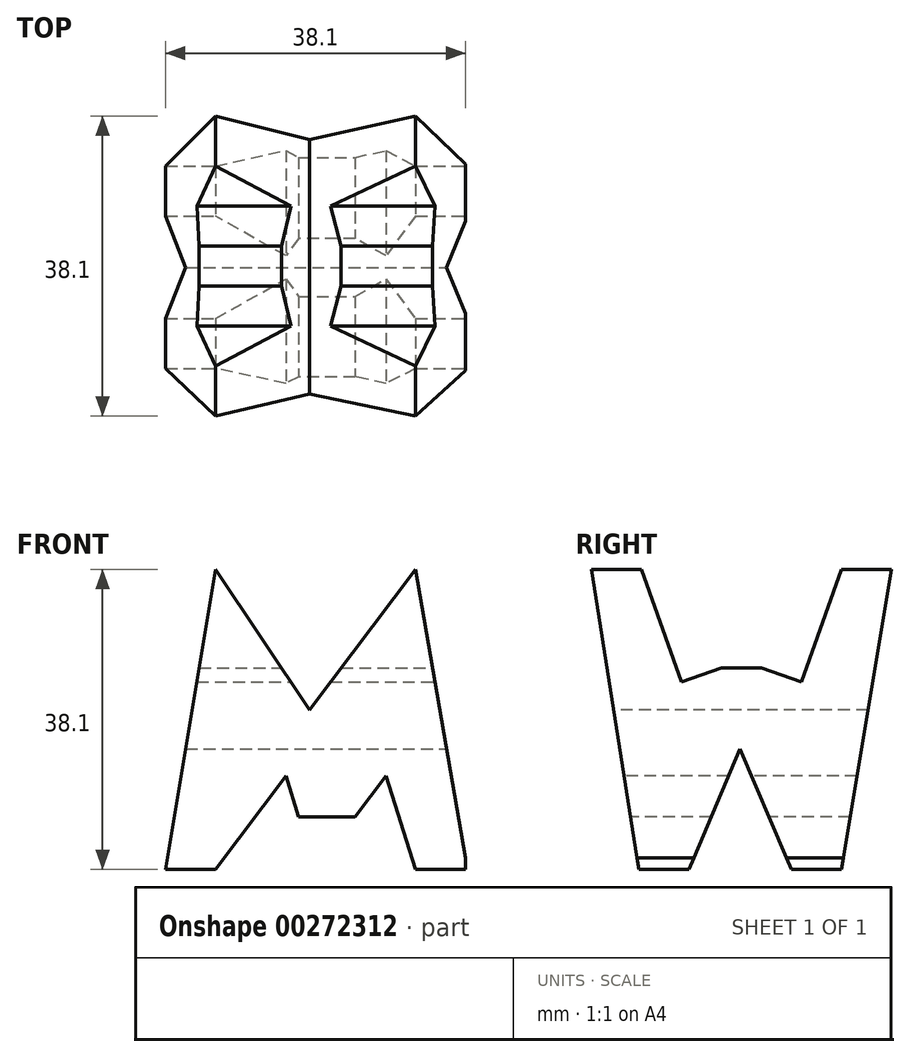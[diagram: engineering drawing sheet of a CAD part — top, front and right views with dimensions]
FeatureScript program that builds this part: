
annotation { "Feature Type Name" : "Feature", "Feature Type Description" : "" }
export const myFeature = defineFeature(function(context is Context, id is Id, definition is map)
    precondition{}
    {
        {
            var Q0;
            Q0=qCreatedBy(makeId("Front.planeOp"),FACE);
            var sketch = newSketch(context, id + "F0", { "sketchPlane" : qUnion([Q0])});
            skLineSegment(sketch, "E0.bottom", {"start": v(0, 0) * mm, "end": v(38.1, 0) * mm});
            skLineSegment(sketch, "E0.top", {"start": v(0, 38.1) * mm, "end": v(38.1, 38.1) * mm});
            skLineSegment(sketch, "E0.left", {"start": v(0, 0) * mm, "end": v(0, 38.1) * mm});
            skLineSegment(sketch, "E0.right", {"start": v(38.1, 0) * mm, "end": v(38.1, 38.1) * mm});
            skSolve(sketch);
        }
        {
            var Q0;
            Q0 = qSketchRegion(id + "F0", true);
            extrude(context, id + "F1", {"entities" : qUnion([Q0]), "depth" : 38.1 * mm});
        }
        {
            var Q0;
            Q0=qCreatedBy(makeId("Front.planeOp"),FACE);
            cPlane(context, id + "F2", {"entities" : qUnion([Q0]), "cplaneType" : CPlaneType.OFFSET, "offset" : 38.1 * mm, "width" : 152.4 * mm, "height" : 152.4 * mm});
        }
        {
            var Q0;
            Q0=qCreatedBy(makeId("Right.planeOp"),FACE);
            cPlane(context, id + "F3", {"entities" : qUnion([Q0]), "cplaneType" : CPlaneType.OFFSET, "offset" : 38.1 * mm, "width" : 152.4 * mm, "height" : 152.4 * mm});
        }
        {
            var Q0;
            Q0=qCreatedBy(id+"F3.planeOp",FACE);
            var sketch = newSketch(context, id + "F4", { "sketchPlane" : qUnion([Q0])});
            skLineSegment(sketch, "E1.bottom", {"start": v(-38.43, 0) * mm, "end": v(0, 0) * mm});
            skLineSegment(sketch, "E1.top", {"start": v(-38.1, 38.1) * mm, "end": v(0, 38.1) * mm});
            skLineSegment(sketch, "E1.left", {"start": v(-38.1, 0) * mm, "end": v(-38.1, 38.1) * mm});
            skLineSegment(sketch, "E1.right", {"start": v(0, 0) * mm, "end": v(0, 38.1) * mm});
            skLineSegment(sketch, "E2", {"start": v(-38.1, 38.1) * mm, "end": v(-32.08, 0) * mm});
            skLineSegment(sketch, "E3", {"start": v(-25.73, 0) * mm, "end": v(-19.21, 15.32) * mm});
            skPoint(sketch, "E3.endSnap0", {"position": v(-19.21, 0) * mm});
            skLineSegment(sketch, "E4", {"start": v(-19.21, 15.32) * mm, "end": v(-12.7, 0) * mm});
            skLineSegment(sketch, "E5", {"start": v(-6.35, 0) * mm, "end": v(0, 38.1) * mm});
            skLineSegment(sketch, "E6", {"start": v(-31.75, 38.1) * mm, "end": v(-26.67, 23.8) * mm});
            skLineSegment(sketch, "E7", {"start": v(-6.35, 38.1) * mm, "end": v(-11.43, 23.8) * mm});
            skLineSegment(sketch, "E8", {"start": v(-26.67, 23.8) * mm, "end": v(-21.6, 25.6) * mm});
            skLineSegment(sketch, "E9", {"start": v(-11.43, 23.8) * mm, "end": v(-16.51, 25.6) * mm});
            skLineSegment(sketch, "E10", {"start": v(-16.51, 25.6) * mm, "end": v(-21.6, 25.6) * mm});
            skSolve(sketch);
        }
        {
            var Q0;
            Q0=qCreatedBy(id+"F2.planeOp",FACE);
            var sketch = newSketch(context, id + "F5", { "sketchPlane" : qUnion([Q0])});
            skPoint(sketch, "E11.endSnap0", {"position": v(30.3, 6.63) * mm});
            skLineSegment(sketch, "E12.bottom", {"start": v(0, 0) * mm, "end": v(38.35, 0) * mm});
            skLineSegment(sketch, "E12.top", {"start": v(0, 37.85) * mm, "end": v(38.35, 37.85) * mm});
            skLineSegment(sketch, "E12.left", {"start": v(0, 0) * mm, "end": v(0, 37.85) * mm});
            skLineSegment(sketch, "E12.right", {"start": v(38.35, 0) * mm, "end": v(38.35, 37.85) * mm});
            skSolve(sketch);
        }
        {
            var Q0;
            {var subQ0=sQuery(id+"F4.wireOp",EDGE,"E1.left");Q0=makeQuery(id+"F4.imprint","IMPRINT",FACE,{"disambiguationData":[TD([[makeQuery(id+"F4.imprint","IMPRINT",EDGE,{"derivedFrom":subQ0}),-1.0]])]});}
            var Q1;
            {var subQ1=sQuery(id+"F4.wireOp",EDGE,"E6");Q1=makeQuery(id+"F4.imprint","IMPRINT",FACE,{"disambiguationData":[TD([[makeQuery(id+"F4.imprint","IMPRINT",EDGE,{"derivedFrom":subQ1}),1.0]])]});}
            var Q2;
            {var subQ0=sQuery(id+"F4.wireOp",EDGE,"E1.right");Q2=makeQuery(id+"F4.imprint","IMPRINT",FACE,{"disambiguationData":[TD([[makeQuery(id+"F4.imprint","IMPRINT",EDGE,{"derivedFrom":subQ0}),1.0]])]});}
            var Q3;
            {var subQ0=sQuery(id+"F4.wireOp",EDGE,"E3");Q3=makeQuery(id+"F4.imprint","IMPRINT",FACE,{"disambiguationData":[TD([[makeQuery(id+"F4.imprint","IMPRINT",EDGE,{"derivedFrom":subQ0}),-1.0]])]});}
            extrude(context, id + "F6", {"entities" : qUnion([Q0, Q1, Q2, Q3]), "operationType" : NewBodyOperationType.REMOVE, "oppositeDirection" : true, "depth" : 38.1 * mm});
        }
        {
            var Q0;
            Q0=qCreatedBy(id+"F2.planeOp",FACE);
            var sketch = newSketch(context, id + "F7", { "sketchPlane" : qUnion([Q0])});
            skLineSegment(sketch, "E13", {"start": v(0, 0) * mm, "end": v(6.35, 38.1) * mm});
            skLineSegment(sketch, "E14", {"start": v(6.35, 38.1) * mm, "end": v(18.29, 20.29) * mm});
            skLineSegment(sketch, "E15", {"start": v(18.29, 20.29) * mm, "end": v(31.75, 38.1) * mm});
            skLineSegment(sketch, "E16", {"start": v(31.75, 38.1) * mm, "end": v(38.35, 0) * mm});
            skLineSegment(sketch, "E17", {"start": v(31.75, 0) * mm, "end": v(28, 11.86) * mm});
            skLineSegment(sketch, "E18", {"start": v(28, 11.86) * mm, "end": v(24.08, 6.66) * mm});
            skLineSegment(sketch, "E19", {"start": v(24.08, 6.66) * mm, "end": v(16.92, 6.66) * mm});
            skLineSegment(sketch, "E20", {"start": v(16.92, 6.66) * mm, "end": v(15.27, 11.86) * mm});
            skLineSegment(sketch, "E21", {"start": v(15.27, 11.86) * mm, "end": v(6.35, 0) * mm});
            skLineSegment(sketch, "E22.bottom", {"start": v(0, 0) * mm, "end": v(38.1, 0) * mm});
            skLineSegment(sketch, "E22.top", {"start": v(0, 38.1) * mm, "end": v(38.1, 38.1) * mm});
            skLineSegment(sketch, "E22.left", {"start": v(0, 0) * mm, "end": v(0, 38.1) * mm});
            skLineSegment(sketch, "E22.right", {"start": v(38.1, 0) * mm, "end": v(38.1, 38.1) * mm});
            skSolve(sketch);
        }
        {
            var Q0;
            {var subQ0=sQuery(id+"F7.wireOp",EDGE,"E13");Q0=makeQuery(id+"F7.imprint","IMPRINT",FACE,{"disambiguationData":[TD([[makeQuery(id+"F7.imprint","IMPRINT",EDGE,{"derivedFrom":subQ0}),1.0]])]});}
            var Q1;
            {var subQ0=sQuery(id+"F7.wireOp",EDGE,"E22.top");var subQ3=sQuery(id+"F7.wireOp",EDGE,"E22.right");var subQ5=makeQuery(id+"F7.imprint","INTERSECT",VERTEX,{"derivedFrom":[subQ0,subQ3]});Q1=makeQuery(id+"F7.imprint","IMPRINT",FACE,{"disambiguationData":[TD([[makeQuery(id+"F7.imprint","IMPRINT",EDGE,{"disambiguationData":[TD([[subQ5,1.0]])],"derivedFrom":subQ3}),1.0]])]});}
            var Q2;
            {var subQ0=sQuery(id+"F7.wireOp",EDGE,"E17");Q2=makeQuery(id+"F7.imprint","IMPRINT",FACE,{"disambiguationData":[TD([[makeQuery(id+"F7.imprint","IMPRINT",EDGE,{"derivedFrom":subQ0}),1.0]])]});}
            var Q3;
            {var subQ0=sQuery(id+"F7.wireOp",EDGE,"E14");Q3=makeQuery(id+"F7.imprint","IMPRINT",FACE,{"disambiguationData":[TD([[makeQuery(id+"F7.imprint","IMPRINT",EDGE,{"derivedFrom":subQ0}),1.0]])]});}
            extrude(context, id + "F8", {"entities" : qUnion([Q0, Q1, Q2, Q3]), "operationType" : NewBodyOperationType.REMOVE, "oppositeDirection" : true, "depth" : 38.1 * mm});
        }
    });
